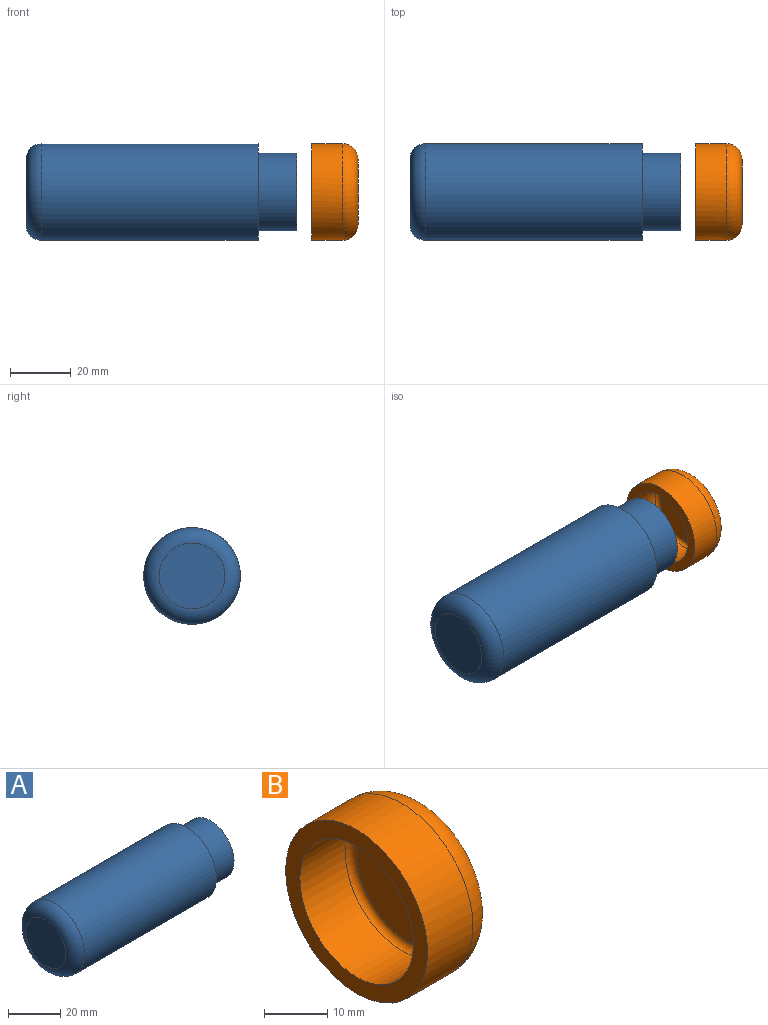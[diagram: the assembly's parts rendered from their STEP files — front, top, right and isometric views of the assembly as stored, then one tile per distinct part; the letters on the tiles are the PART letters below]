
ASSEMBLY  parts=2 mates=1
PART A: 8 faces, bbox 88.9x34.4x34.4 mm
  f0: plane 25.4x25.4mm, normal (1,0,0), area 182.4mm2, adj f1,f4
  f1: cylinder r=10.16mm len=77.95mm, axis (-1,0,0), area 4976.4mm2, adj f0,f2
  f2: cone r=0mm half-angle=60deg, axis (1,0,0), area 374.5mm2, adj f1
  f3: plane 31.75x31.75mm, normal (1,0,0), area 285mm2, adj f4,f7
  f4: cylinder r=12.7mm len=25.4mm, axis (1,0,0), area 1013.4mm2, adj f0,f3
  f5: plane 21.59x21.59mm, normal (-1,0,0), area 366.1mm2, adj f6
  f6: torus R=10.79mm, axis (1,0,0), area 703.4mm2, adj f5,f7
  f7: cylinder r=15.88mm len=71.12mm, axis (1,0,0), area 7093.9mm2, adj f3,f6
PART B: 8 faces, bbox 15.2x34.4x34.4 mm
  f0: cylinder r=15.88mm len=31.75mm, axis (-1,0,0), area 1013.4mm2, adj f2,f3
  f1: plane 21.59x21.59mm, normal (1,0,0), area 366.1mm2, adj f3
  f2: plane 31.75x31.75mm, normal (-1,0,0), area 285mm2, adj f0,f6
  f3: torus R=10.79mm, axis (1,0,0), area 703.4mm2, adj f0,f1
  f4: plane 22.86x22.86mm, normal (-1,0,0), area 395.2mm2, adj f5,f7
  f5: torus R=11.43mm, axis (1,0,0), area 153.4mm2, adj f4,f6
  f6: cylinder r=12.7mm len=25.4mm, axis (1,0,0), area 810.7mm2, adj f2,f5
  f7: cone r=2.2mm half-angle=60deg, axis (-1,0,0), area 17.6mm2, adj f4
PLACE A t=(-15.03,-30.95,26.81)mm
PLACE B t=(-10.17,-30.95,26.81)mm
MATE cylindrical A.f1 <-> B.f6  axis (1,0,0) through (-21.38,-30.95,26.81)mm
